# Revit family: Sanitary_Napkin_Disposal-Bobrick-B-9254_Series
name_source: partatom
category: Specialty Equipment
units: mm (PartAtom-declared; Revit-internal decimal feet)

## family parameters
Cut with Voids When Loaded = No
Host = Face
OmniClass Number = 23.40.20.21.24
OmniClass Title = Sanitary Napkin and Tampon Dispensers, Disposal Units
Part Type = Normal
Room Calculation Point = No
Round Connector Dimension = Use Diameter
Shared = Yes

## types (2) — shared parameters
ADA Compliant = Yes
Assembly Code = E1090900
Capacity = Capacity: 0.8-gal. (3.0-L)
Default Elevation = 0"
Description = Surface Mounted Sanitary Disposal
Height = 13"
Installation Type = Surface Mounted
Length = 7 1/2"
Manufacturer = Bobrick
Mounting Height = 29"
URL = https://www.bobrick.com
Warranty Information = 5-Year Limited Warranty — In addition to Bobrick’s one-year guarantee, Bobrick extends a limited 5-year
warranty from the date of purchase on all parts for model B-9254.
Waste Receptacle Replacement 9254-20 = No
Width = 4 1/4"

## per-type parameters (varying)
| type | Finish | Material |
| B-9254 | Stainless Steel-Bobrick-Satin | Stainless Steel-Bobrick-Satin |
| B-9254.MBLK | Stainless Steel-Bobrick-Matte Black | Stainless Steel-Bobrick-Matte Black |

note: column(s) folded — value = type name in every type: Model

## geometry (parser evidence)
native form markers: Sweep x3
no freeform markers — native parametric forms only
